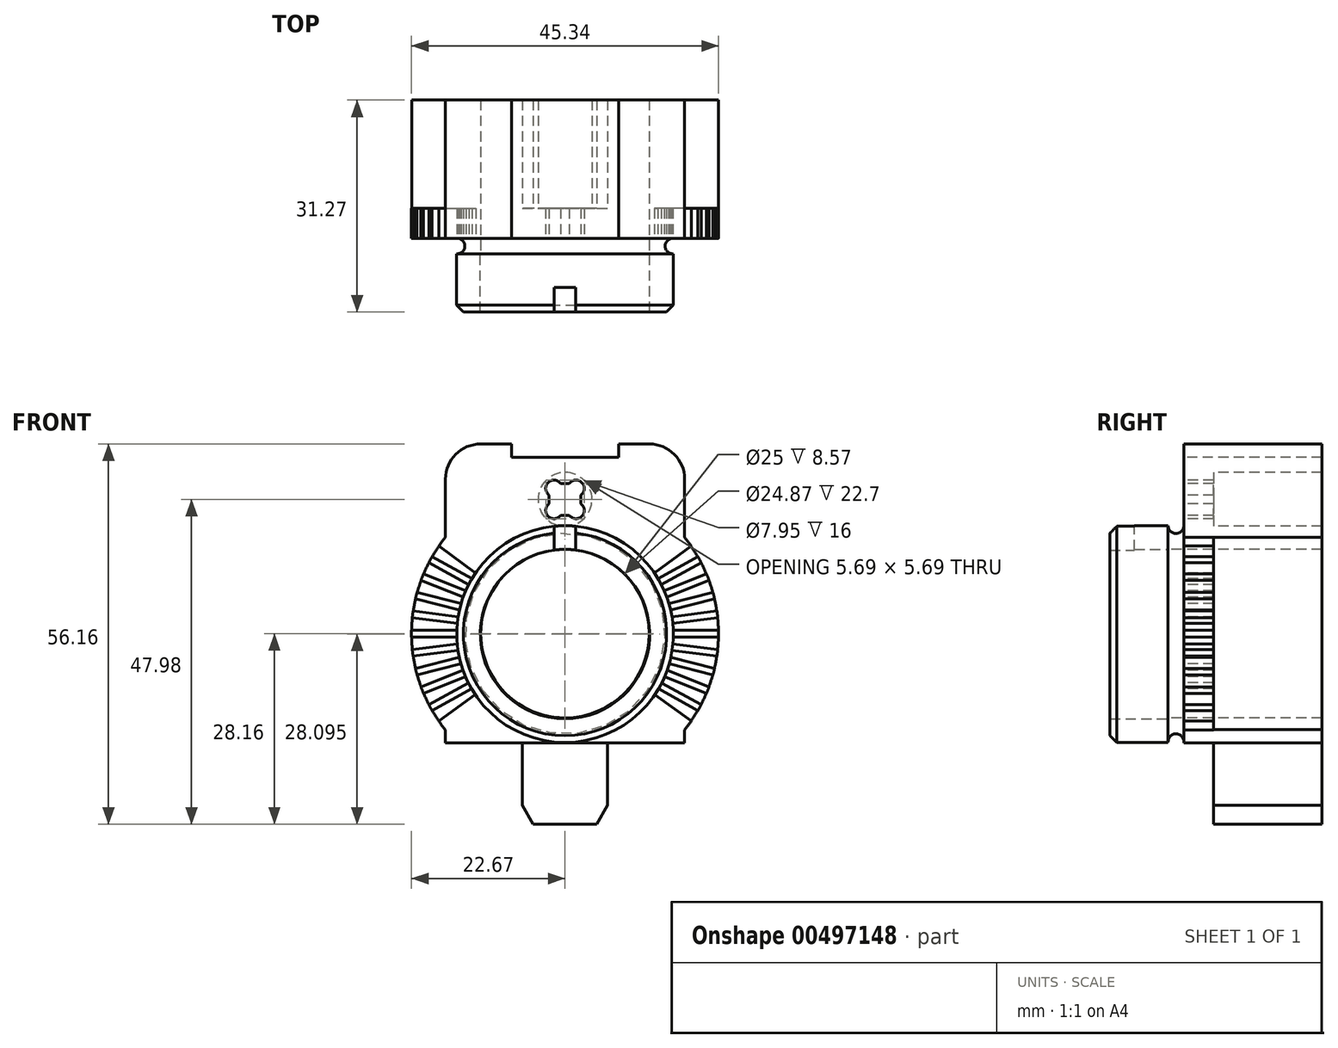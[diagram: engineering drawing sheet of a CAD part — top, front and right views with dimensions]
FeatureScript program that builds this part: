
annotation { "Feature Type Name" : "Feature", "Feature Type Description" : "" }
export const myFeature = defineFeature(function(context is Context, id is Id, definition is map)
    precondition{}
    {
        {
            var Q0;
            Q0=qCreatedBy(makeId("Front.planeOp"),FACE);
            var sketch = newSketch(context, id + "F0", { "sketchPlane" : qUnion([Q0])});
            skArc(sketch, "E0", {"start": v(-1.6, 12.33) * mm, "mid": v(0, -12.56) * mm, "end": v(1.6, 12.33) * mm});
            skArc(sketch, "E1", {"start": v(-1.6, 15.85) * mm, "mid": v(0, -16.06) * mm, "end": v(1.6, 15.85) * mm});
            skLineSegment(sketch, "E2.0", {"start": v(-1.6, 12.33) * mm, "end": v(-1.6, 15.85) * mm});
            skArc(sketch, "E3", {"start": v(1.6, 12.33) * mm, "mid": v(0, 12.44) * mm, "end": v(-1.6, 12.33) * mm});
            skArc(sketch, "E4", {"start": v(1.6, 15.85) * mm, "mid": v(0, 15.94) * mm, "end": v(-1.6, 15.85) * mm});
            skLineSegment(sketch, "E5", {"start": v(1.6, 12.33) * mm, "end": v(1.6, 15.85) * mm});
            skSolve(sketch);
        }
        {
            var Q0;
            Q0=makeQuery(id+"F0.imprint","IMPRINT",FACE,{"disambiguationData":[TD([[makeQuery(id+"F0.imprint","IMPRINT",EDGE,{"derivedFrom":sQuery(id+"F0.wireOp",EDGE,"E0")}),-1.0]])]});
            extrude(context, id + "F1", {"entities" : qUnion([Q0]), "depth" : 8.57 * mm});
        }
        {
            var Q0;
            Q0=makeQuery(id+"F0.imprint","IMPRINT",FACE,{"disambiguationData":[TD([[makeQuery(id+"F0.imprint","IMPRINT",EDGE,{"derivedFrom":sQuery(id+"F0.wireOp",EDGE,"E2.0")}),-1.0]])]});
            extrude(context, id + "F2", {"entities" : qUnion([Q0]), "operationType" : NewBodyOperationType.ADD, "depth" : 4.97 * mm});
        }
        {
            var Q0;
            Q0=qCreatedBy(makeId("Right.planeOp"),FACE);
            var sketch = newSketch(context, id + "F3", { "sketchPlane" : qUnion([Q0])});
            skLineSegment(sketch, "E6", {"start": v(2.3, 15.94) * mm, "end": v(2.3, 12.44) * mm});
            skLineSegment(sketch, "E7", {"start": v(0, 12.44) * mm, "end": v(2.3, 12.44) * mm});
            skLineSegment(sketch, "E8", {"start": v(0, 0) * mm, "end": v(5.15, 0) * mm});
            skArc(sketch, "E9", {"start": v(0, 15.94) * mm, "mid": v(1.15, 14.79) * mm, "end": v(2.3, 15.94) * mm});
            skLineSegment(sketch, "E10", {"start": v(0, 12.44) * mm, "end": v(0, 15.94) * mm});
            skSolve(sketch);
        }
        {
            var Q0;
            Q0=makeQuery(id+"F3.imprint","IMPRINT",FACE,{"disambiguationData":[TD([[makeQuery(id+"F3.imprint","IMPRINT",EDGE,{"derivedFrom":sQuery(id+"F3.wireOp",EDGE,"E6")}),-1.0]])]});
            var Q1;
            Q1=sQuery(id+"F3.wireOp",EDGE,"E8");
            revolve(context, id + "F4", {"operationType" : NewBodyOperationType.ADD, "entities" : qUnion([Q0]), "axis" : qUnion([Q1]), "revolveType" : RevolveType.FULL});
        }
        {
            var Q0;
            Q0=makeQuery(id+"F4.opRevolve","SWEPT_FACE",FACE,{"disambiguationData":[OSD([sQuery(id+"F3.wireOp",EDGE,"E6")])]});
            var sketch = newSketch(context, id + "F5", { "sketchPlane" : qUnion([Q0])});
            skArc(sketch, "E11", {"start": v(17.65, 22.8) * mm, "mid": v(16.13, 26.48) * mm, "end": v(12.45, 28) * mm});
            skArc(sketch, "E12.MirrorCS", {"start": v(-17.65, 22.8) * mm, "mid": v(-16.13, 26.48) * mm, "end": v(-12.45, 28) * mm});
            skLineSegment(sketch, "E13", {"start": v(-17.65, 22.8) * mm, "end": v(-17.65, 14.23) * mm});
            skLineSegment(sketch, "E14", {"start": v(17.65, 22.8) * mm, "end": v(17.65, 14.23) * mm});
            skLineSegment(sketch, "E15.trimOffspring", {"start": v(17.65, -14.23) * mm, "end": v(17.65, -16.16) * mm});
            skLineSegment(sketch, "E16.trimOffspring", {"start": v(-17.65, -14.23) * mm, "end": v(-17.65, -16.16) * mm});
            skLineSegment(sketch, "E17", {"start": v(-12.45, 28) * mm, "end": v(-7.9, 28) * mm});
            skCircle(sketch, "E18", {"center": v(0, 0) * mm, "radius": 12.44 * mm});
            skLineSegment(sketch, "E19.top", {"start": v(-0.64, 17.47) * mm, "end": v(0.64, 17.47) * mm});
            skLineSegment(sketch, "E19.right", {"start": v(2.35, 20.46) * mm, "end": v(2.35, 19.18) * mm});
            skArc(sketch, "E20", {"start": v(-0.64, 22.17) * mm, "mid": v(-2.49, 22.3) * mm, "end": v(-2.35, 20.46) * mm});
            skArc(sketch, "E21.MirrorC", {"start": v(-0.64, 17.47) * mm, "mid": v(-2.49, 17.33) * mm, "end": v(-2.35, 19.18) * mm});
            skArc(sketch, "E22.MirrorC", {"start": v(0.64, 22.17) * mm, "mid": v(2.49, 22.3) * mm, "end": v(2.35, 20.46) * mm});
            skArc(sketch, "E23.MirrorC", {"start": v(0.64, 17.47) * mm, "mid": v(2.49, 17.33) * mm, "end": v(2.35, 19.18) * mm});
            skLineSegment(sketch, "E24", {"start": v(0.64, 22.17) * mm, "end": v(-0.64, 22.17) * mm});
            skLineSegment(sketch, "E25.trimOffspring", {"start": v(-2.35, 19.18) * mm, "end": v(-2.35, 20.46) * mm});
            skLineSegment(sketch, "E26.0", {"start": v(-7.9, 28) * mm, "end": v(-7.9, 26) * mm});
            skLineSegment(sketch, "E27.0", {"start": v(7.9, 28) * mm, "end": v(7.9, 26) * mm});
            skLineSegment(sketch, "E28", {"start": v(-7.9, 26) * mm, "end": v(7.9, 26) * mm});
            skLineSegment(sketch, "E29", {"start": v(-6.3, -25.36) * mm, "end": v(6.3, -25.36) * mm});
            skLineSegment(sketch, "E30", {"start": v(-4.7, -28.16) * mm, "end": v(4.7, -28.16) * mm});
            skLineSegment(sketch, "E31", {"start": v(-4.7, -28.16) * mm, "end": v(-6.3, -25.36) * mm});
            skLineSegment(sketch, "E32.MirrorCS", {"start": v(6.3, -16.16) * mm, "end": v(6.3, -25.36) * mm});
            skLineSegment(sketch, "E33.MirrorCS", {"start": v(4.7, -28.16) * mm, "end": v(6.3, -25.36) * mm});
            skLineSegment(sketch, "E34", {"start": v(-6.3, -25.36) * mm, "end": v(-6.3, -16.16) * mm});
            skLineSegment(sketch, "E35", {"start": v(-6.3, -16.16) * mm, "end": v(6.3, -16.16) * mm});
            skLineSegment(sketch, "E36", {"start": v(6.3, -16.16) * mm, "end": v(17.65, -16.16) * mm});
            skLineSegment(sketch, "E37", {"start": v(-6.3, -16.16) * mm, "end": v(-17.65, -16.16) * mm});
            skLineSegment(sketch, "E38.0", {"start": v(22.67, 0.5) * mm, "end": v(15.93, 0.5) * mm});
            skLineSegment(sketch, "E39.0", {"start": v(22.67, -0.5) * mm, "end": v(15.93, -0.5) * mm});
            skLineSegment(sketch, "E40.1.0", {"start": v(22.55, 2.34) * mm, "end": v(15.86, 1.5) * mm});
            skLineSegment(sketch, "E40.1.1", {"start": v(22.43, 3.34) * mm, "end": v(15.74, 2.5) * mm});
            skLineSegment(sketch, "E40.2.0", {"start": v(22.08, 5.15) * mm, "end": v(15.55, 3.48) * mm});
            skLineSegment(sketch, "E40.2.1", {"start": v(21.83, 6.12) * mm, "end": v(15.3, 4.45) * mm});
            skLineSegment(sketch, "E40.3.0", {"start": v(21.26, 7.88) * mm, "end": v(15, 5.4) * mm});
            skLineSegment(sketch, "E40.3.1", {"start": v(20.9, 8.8) * mm, "end": v(14.62, 6.33) * mm});
            skLineSegment(sketch, "E40.4.0", {"start": v(20.1, 10.48) * mm, "end": v(14.2, 7.23) * mm});
            skLineSegment(sketch, "E40.4.1", {"start": v(19.62, 11.36) * mm, "end": v(13.72, 8.11) * mm});
            skLineSegment(sketch, "E40.5.0", {"start": v(18.63, 12.92) * mm, "end": v(13.18, 8.96) * mm});
            skLineSegment(sketch, "E40.21.0", {"start": v(-19.62, 11.36) * mm, "end": v(-13.72, 8.11) * mm});
            skLineSegment(sketch, "E40.21.1", {"start": v(-20.1, 10.48) * mm, "end": v(-14.2, 7.23) * mm});
            skLineSegment(sketch, "E40.22.0", {"start": v(-20.9, 8.8) * mm, "end": v(-14.62, 6.33) * mm});
            skLineSegment(sketch, "E40.22.1", {"start": v(-21.26, 7.88) * mm, "end": v(-15, 5.4) * mm});
            skLineSegment(sketch, "E40.23.0", {"start": v(-21.83, 6.12) * mm, "end": v(-15.3, 4.45) * mm});
            skLineSegment(sketch, "E40.23.1", {"start": v(-22.08, 5.15) * mm, "end": v(-15.55, 3.48) * mm});
            skLineSegment(sketch, "E40.24.0", {"start": v(-22.43, 3.34) * mm, "end": v(-15.74, 2.5) * mm});
            skLineSegment(sketch, "E40.24.1", {"start": v(-22.55, 2.34) * mm, "end": v(-15.86, 1.5) * mm});
            skLineSegment(sketch, "E40.25.0", {"start": v(-22.67, 0.5) * mm, "end": v(-15.93, 0.5) * mm});
            skLineSegment(sketch, "E40.25.1", {"start": v(-22.67, -0.5) * mm, "end": v(-15.93, -0.5) * mm});
            skLineSegment(sketch, "E40.26.0", {"start": v(-22.55, -2.34) * mm, "end": v(-15.86, -1.5) * mm});
            skLineSegment(sketch, "E40.26.1", {"start": v(-22.43, -3.34) * mm, "end": v(-15.74, -2.5) * mm});
            skLineSegment(sketch, "E40.27.0", {"start": v(-22.08, -5.15) * mm, "end": v(-15.55, -3.48) * mm});
            skLineSegment(sketch, "E40.27.1", {"start": v(-21.83, -6.12) * mm, "end": v(-15.3, -4.45) * mm});
            skLineSegment(sketch, "E40.28.0", {"start": v(-21.26, -7.88) * mm, "end": v(-15, -5.4) * mm});
            skLineSegment(sketch, "E40.28.1", {"start": v(-20.9, -8.8) * mm, "end": v(-14.62, -6.33) * mm});
            skLineSegment(sketch, "E40.29.0", {"start": v(-20.1, -10.48) * mm, "end": v(-14.2, -7.23) * mm});
            skLineSegment(sketch, "E40.29.1", {"start": v(-19.62, -11.36) * mm, "end": v(-13.72, -8.11) * mm});
            skLineSegment(sketch, "E40.45.1", {"start": v(18.63, -12.92) * mm, "end": v(13.18, -8.96) * mm});
            skLineSegment(sketch, "E40.46.0", {"start": v(19.62, -11.36) * mm, "end": v(13.72, -8.11) * mm});
            skLineSegment(sketch, "E40.46.1", {"start": v(20.1, -10.48) * mm, "end": v(14.2, -7.23) * mm});
            skLineSegment(sketch, "E40.47.0", {"start": v(20.9, -8.8) * mm, "end": v(14.62, -6.33) * mm});
            skLineSegment(sketch, "E40.47.1", {"start": v(21.26, -7.88) * mm, "end": v(15, -5.4) * mm});
            skLineSegment(sketch, "E40.48.0", {"start": v(21.83, -6.12) * mm, "end": v(15.3, -4.45) * mm});
            skLineSegment(sketch, "E40.48.1", {"start": v(22.08, -5.15) * mm, "end": v(15.55, -3.48) * mm});
            skLineSegment(sketch, "E40.49.0", {"start": v(22.43, -3.34) * mm, "end": v(15.74, -2.5) * mm});
            skLineSegment(sketch, "E40.49.1", {"start": v(22.55, -2.34) * mm, "end": v(15.86, -1.5) * mm});
            skLineSegment(sketch, "E41.MirrorCS", {"start": v(-18.63, -12.92) * mm, "end": v(-13.18, -8.96) * mm});
            skLineSegment(sketch, "E42.MirrorCS", {"start": v(-18.63, 12.92) * mm, "end": v(-13.18, 8.96) * mm});
            skLineSegment(sketch, "E43.trimOffspring", {"start": v(7.9, 28) * mm, "end": v(12.45, 28) * mm});
            skArc(sketch, "E44.trimOffspring", {"start": v(-17.65, 14.23) * mm, "mid": v(-22.67, 0) * mm, "end": v(-17.65, -14.23) * mm});
            skArc(sketch, "E45.trimOffspring", {"start": v(17.65, -14.23) * mm, "mid": v(22.67, 0) * mm, "end": v(17.65, 14.23) * mm});
            skArc(sketch, "E46", {"start": v(15.86, 1.5) * mm, "mid": v(15.8, 2) * mm, "end": v(15.74, 2.5) * mm});
            skPoint(sketch, "E47.orphan", {"position": v(13.18, 8.96) * mm});
            skPoint(sketch, "E48.orphan", {"position": v(13.72, 8.11) * mm});
            skArc(sketch, "E49.trimOffspring", {"start": v(15.93, -0.5) * mm, "mid": v(15.94, 0) * mm, "end": v(15.93, 0.5) * mm});
            skArc(sketch, "E50.trimOffspring", {"start": v(15.74, -2.5) * mm, "mid": v(15.8, -2) * mm, "end": v(15.86, -1.5) * mm});
            skArc(sketch, "E51.trimOffspring", {"start": v(15.3, -4.45) * mm, "mid": v(15.43, -3.96) * mm, "end": v(15.55, -3.48) * mm});
            skArc(sketch, "E52.trimOffspring", {"start": v(14.62, -6.33) * mm, "mid": v(14.82, -5.87) * mm, "end": v(15, -5.4) * mm});
            skArc(sketch, "E53.trimOffspring", {"start": v(13.72, -8.11) * mm, "mid": v(13.96, -7.68) * mm, "end": v(14.2, -7.23) * mm});
            skArc(sketch, "E54.trimOffspring", {"start": v(15.55, 3.48) * mm, "mid": v(15.43, 3.96) * mm, "end": v(15.3, 4.45) * mm});
            skArc(sketch, "E55.trimOffspring", {"start": v(15, 5.4) * mm, "mid": v(14.82, 5.87) * mm, "end": v(14.62, 6.33) * mm});
            skArc(sketch, "E56.trimOffspring", {"start": v(14.2, 7.23) * mm, "mid": v(13.96, 7.68) * mm, "end": v(13.72, 8.11) * mm});
            skArc(sketch, "E57.trimOffspring", {"start": v(13.18, 8.96) * mm, "mid": v(-15.94, 0) * mm, "end": v(13.18, -8.96) * mm});
            skSolve(sketch);
        }
        {
            var Q0;
            Q0=makeQuery(id+"F1.opExtrude","CAP_EDGE",EDGE,{"disambiguationData":[OSD([sQuery(id+"F0.wireOp",EDGE,"E1")])],"isStart":false});
            chamfer(context, id + "F6", {"entities" : qUnion([Q0]), "width" : 1 * mm, "tangentPropagation" : true});
        }
        {
            var Q0;
            Q0=makeQuery(id+"F5.imprint","IMPRINT",FACE,{"disambiguationData":[TD([[makeQuery(id+"F5.imprint","IMPRINT",EDGE,{"derivedFrom":sQuery(id+"F5.wireOp",EDGE,"E18")}),1.0]])]});
            var Q1;
            {var subQ0=sQuery(id+"F5.wireOp",EDGE,"E40.4.0");Q1=makeQuery(id+"F5.imprint","IMPRINT",FACE,{"disambiguationData":[TD([[makeQuery(id+"F5.imprint","IMPRINT",EDGE,{"derivedFrom":subQ0}),-1.0]])]});}
            var Q2;
            {var subQ0=sQuery(id+"F5.wireOp",EDGE,"E40.3.0");Q2=makeQuery(id+"F5.imprint","IMPRINT",FACE,{"disambiguationData":[TD([[makeQuery(id+"F5.imprint","IMPRINT",EDGE,{"derivedFrom":subQ0}),-1.0]])]});}
            var Q3;
            {var subQ0=sQuery(id+"F5.wireOp",EDGE,"E40.2.0");Q3=makeQuery(id+"F5.imprint","IMPRINT",FACE,{"disambiguationData":[TD([[makeQuery(id+"F5.imprint","IMPRINT",EDGE,{"derivedFrom":subQ0}),-1.0]])]});}
            var Q4;
            {var subQ0=sQuery(id+"F5.wireOp",EDGE,"E40.1.0");Q4=makeQuery(id+"F5.imprint","IMPRINT",FACE,{"disambiguationData":[TD([[makeQuery(id+"F5.imprint","IMPRINT",EDGE,{"derivedFrom":subQ0}),-1.0]])]});}
            var Q5;
            {var subQ0=sQuery(id+"F5.wireOp",EDGE,"E38.0");Q5=makeQuery(id+"F5.imprint","IMPRINT",FACE,{"disambiguationData":[TD([[makeQuery(id+"F5.imprint","IMPRINT",EDGE,{"derivedFrom":subQ0}),1.0]])]});}
            var Q6;
            {var subQ0=sQuery(id+"F5.wireOp",EDGE,"E40.49.0");Q6=makeQuery(id+"F5.imprint","IMPRINT",FACE,{"disambiguationData":[TD([[makeQuery(id+"F5.imprint","IMPRINT",EDGE,{"derivedFrom":subQ0}),-1.0]])]});}
            var Q7;
            {var subQ0=sQuery(id+"F5.wireOp",EDGE,"E40.48.0");Q7=makeQuery(id+"F5.imprint","IMPRINT",FACE,{"disambiguationData":[TD([[makeQuery(id+"F5.imprint","IMPRINT",EDGE,{"derivedFrom":subQ0}),-1.0]])]});}
            var Q8;
            {var subQ0=sQuery(id+"F5.wireOp",EDGE,"E40.47.0");Q8=makeQuery(id+"F5.imprint","IMPRINT",FACE,{"disambiguationData":[TD([[makeQuery(id+"F5.imprint","IMPRINT",EDGE,{"derivedFrom":subQ0}),-1.0]])]});}
            var Q9;
            {var subQ0=sQuery(id+"F5.wireOp",EDGE,"E40.46.0");Q9=makeQuery(id+"F5.imprint","IMPRINT",FACE,{"disambiguationData":[TD([[makeQuery(id+"F5.imprint","IMPRINT",EDGE,{"derivedFrom":subQ0}),-1.0]])]});}
            var Q10;
            {var subQ0=sQuery(id+"F5.wireOp",EDGE,"E15.trimOffspring");Q10=makeQuery(id+"F5.imprint","IMPRINT",FACE,{"disambiguationData":[TD([[makeQuery(id+"F5.imprint","IMPRINT",EDGE,{"derivedFrom":subQ0}),-1.0]])]});}
            var Q11;
            {var subQ0=sQuery(id+"F5.wireOp",EDGE,"E40.21.0");Q11=makeQuery(id+"F5.imprint","IMPRINT",FACE,{"disambiguationData":[TD([[makeQuery(id+"F5.imprint","IMPRINT",EDGE,{"derivedFrom":subQ0}),-1.0]])]});}
            var Q12;
            {var subQ0=sQuery(id+"F5.wireOp",EDGE,"E40.22.0");Q12=makeQuery(id+"F5.imprint","IMPRINT",FACE,{"disambiguationData":[TD([[makeQuery(id+"F5.imprint","IMPRINT",EDGE,{"derivedFrom":subQ0}),-1.0]])]});}
            var Q13;
            {var subQ0=sQuery(id+"F5.wireOp",EDGE,"E40.23.0");Q13=makeQuery(id+"F5.imprint","IMPRINT",FACE,{"disambiguationData":[TD([[makeQuery(id+"F5.imprint","IMPRINT",EDGE,{"derivedFrom":subQ0}),-1.0]])]});}
            var Q14;
            {var subQ0=sQuery(id+"F5.wireOp",EDGE,"E40.24.0");Q14=makeQuery(id+"F5.imprint","IMPRINT",FACE,{"disambiguationData":[TD([[makeQuery(id+"F5.imprint","IMPRINT",EDGE,{"derivedFrom":subQ0}),-1.0]])]});}
            var Q15;
            {var subQ0=sQuery(id+"F5.wireOp",EDGE,"E40.25.0");Q15=makeQuery(id+"F5.imprint","IMPRINT",FACE,{"disambiguationData":[TD([[makeQuery(id+"F5.imprint","IMPRINT",EDGE,{"derivedFrom":subQ0}),-1.0]])]});}
            var Q16;
            {var subQ0=sQuery(id+"F5.wireOp",EDGE,"E40.26.0");Q16=makeQuery(id+"F5.imprint","IMPRINT",FACE,{"disambiguationData":[TD([[makeQuery(id+"F5.imprint","IMPRINT",EDGE,{"derivedFrom":subQ0}),-1.0]])]});}
            var Q17;
            {var subQ0=sQuery(id+"F5.wireOp",EDGE,"E40.27.0");Q17=makeQuery(id+"F5.imprint","IMPRINT",FACE,{"disambiguationData":[TD([[makeQuery(id+"F5.imprint","IMPRINT",EDGE,{"derivedFrom":subQ0}),-1.0]])]});}
            var Q18;
            {var subQ0=sQuery(id+"F5.wireOp",EDGE,"E40.28.0");Q18=makeQuery(id+"F5.imprint","IMPRINT",FACE,{"disambiguationData":[TD([[makeQuery(id+"F5.imprint","IMPRINT",EDGE,{"derivedFrom":subQ0}),-1.0]])]});}
            var Q19;
            {var subQ0=sQuery(id+"F5.wireOp",EDGE,"E40.29.0");Q19=makeQuery(id+"F5.imprint","IMPRINT",FACE,{"disambiguationData":[TD([[makeQuery(id+"F5.imprint","IMPRINT",EDGE,{"derivedFrom":subQ0}),-1.0]])]});}
            var Q20;
            Q20=makeQuery(id+"F5.imprint","IMPRINT",FACE,{"disambiguationData":[TD([[makeQuery(id+"F5.imprint","IMPRINT",EDGE,{"derivedFrom":sQuery(id+"F5.wireOp",EDGE,"E11")}),1.0]])]});
            extrude(context, id + "F7", {"entities" : qUnion([Q0, Q1, Q2, Q3, Q4, Q5, Q6, Q7, Q8, Q9, Q10, Q11, Q12, Q13, Q14, Q15, Q16, Q17, Q18, Q19, Q20]), "operationType" : NewBodyOperationType.ADD, "depth" : 4.4 * mm});
        }
        {
            var Q0;
            Q0=makeQuery(id+"F7.opExtrude","CAP_FACE",FACE,{"disambiguationData":[OSD([sQuery(id+"F5.wireOp",EDGE,"E11"),sQuery(id+"F5.wireOp",EDGE,"E12.MirrorCS"),sQuery(id+"F5.wireOp",EDGE,"E13"),sQuery(id+"F5.wireOp",EDGE,"E14"),sQuery(id+"F5.wireOp",EDGE,"42445285-0d22-4fb7-9066-266c46115e63"),sQuery(id+"F5.wireOp",EDGE,"E15.trimOffspring"),sQuery(id+"F5.wireOp",EDGE,"E16.trimOffspring"),sQuery(id+"F5.wireOp",EDGE,"E17"),sQuery(id+"F5.wireOp",EDGE,"17f85dbb-1fbd-415c-9f06-a603da59e3970.MirrorCS"),sQuery(id+"F5.wireOp",EDGE,"E18"),sQuery(id+"F5.wireOp",EDGE,"E19.top"),sQuery(id+"F5.wireOp",EDGE,"E19.right"),sQuery(id+"F5.wireOp",EDGE,"E20"),sQuery(id+"F5.wireOp",EDGE,"E21.MirrorC"),sQuery(id+"F5.wireOp",EDGE,"E22.MirrorC"),sQuery(id+"F5.wireOp",EDGE,"E23.MirrorC"),sQuery(id+"F5.wireOp",EDGE,"E24"),sQuery(id+"F5.wireOp",EDGE,"E25.trimOffspring"),sQuery(id+"F5.wireOp",EDGE,"E30"),sQuery(id+"F5.wireOp",EDGE,"E31"),sQuery(id+"F5.wireOp",EDGE,"E32.MirrorCS"),sQuery(id+"F5.wireOp",EDGE,"E33.MirrorCS"),sQuery(id+"F5.wireOp",EDGE,"E34"),sQuery(id+"F5.wireOp",EDGE,"E36"),sQuery(id+"F5.wireOp",EDGE,"E37")])],"isStart":false});
            var sketch = newSketch(context, id + "F8", { "sketchPlane" : qUnion([Q0])});
            skArc(sketch, "E58", {"start": v(17.65, 22.8) * mm, "mid": v(16.13, 26.48) * mm, "end": v(12.45, 28) * mm});
            skArc(sketch, "E59.MirrorCS", {"start": v(-17.65, 22.8) * mm, "mid": v(-16.13, 26.48) * mm, "end": v(-12.45, 28) * mm});
            skLineSegment(sketch, "E60", {"start": v(-17.65, 22.8) * mm, "end": v(-17.65, 14.2) * mm});
            skLineSegment(sketch, "E61", {"start": v(17.65, 22.8) * mm, "end": v(17.65, 14.2) * mm});
            skArc(sketch, "E62", {"start": v(-17.65, 14.2) * mm, "mid": v(-22.65, 0) * mm, "end": v(-17.65, -14.2) * mm});
            skLineSegment(sketch, "E63.trimOffspring", {"start": v(17.65, -14.2) * mm, "end": v(17.65, -16.16) * mm});
            skLineSegment(sketch, "E64.trimOffspring", {"start": v(-17.65, -14.2) * mm, "end": v(-17.65, -16.16) * mm});
            skLineSegment(sketch, "E65", {"start": v(-12.45, 28) * mm, "end": v(-7.9, 28) * mm});
            skArc(sketch, "E66.MirrorCS", {"start": v(17.65, 14.2) * mm, "mid": v(22.65, 0) * mm, "end": v(17.65, -14.2) * mm});
            skCircle(sketch, "E67", {"center": v(0, 0) * mm, "radius": 12.44 * mm});
            skLineSegment(sketch, "E68.0", {"start": v(-7.9, 28) * mm, "end": v(-7.9, 26) * mm});
            skLineSegment(sketch, "E69.0", {"start": v(7.9, 28) * mm, "end": v(7.9, 26) * mm});
            skLineSegment(sketch, "E70", {"start": v(-7.9, 26) * mm, "end": v(7.9, 26) * mm});
            skLineSegment(sketch, "E71", {"start": v(-6.3, -25.36) * mm, "end": v(6.3, -25.36) * mm});
            skLineSegment(sketch, "E72", {"start": v(-4.7, -28.16) * mm, "end": v(4.7, -28.16) * mm});
            skLineSegment(sketch, "E73", {"start": v(-4.7, -28.16) * mm, "end": v(-6.3, -25.36) * mm});
            skLineSegment(sketch, "E74.MirrorCS", {"start": v(6.3, -16.16) * mm, "end": v(6.3, -25.36) * mm});
            skLineSegment(sketch, "E75.MirrorCS", {"start": v(4.7, -28.16) * mm, "end": v(6.3, -25.36) * mm});
            skLineSegment(sketch, "E76", {"start": v(-6.3, -25.36) * mm, "end": v(-6.3, -16.16) * mm});
            skLineSegment(sketch, "E77", {"start": v(-6.3, -16.16) * mm, "end": v(6.3, -16.16) * mm});
            skLineSegment(sketch, "E78", {"start": v(6.3, -16.16) * mm, "end": v(17.65, -16.16) * mm});
            skLineSegment(sketch, "E79", {"start": v(-6.3, -16.16) * mm, "end": v(-17.65, -16.16) * mm});
            skCircle(sketch, "E80", {"center": v(0, 19.82) * mm, "radius": 3.98 * mm});
            skLineSegment(sketch, "E81.trimOffspring", {"start": v(7.9, 28) * mm, "end": v(12.45, 28) * mm});
            skSolve(sketch);
        }
        {
            var Q0;
            Q0 = qSketchRegion(id + "F8", true);
            extrude(context, id + "F9", {"entities" : qUnion([Q0]), "operationType" : NewBodyOperationType.ADD, "depth" : 16 * mm});
        }
    });
